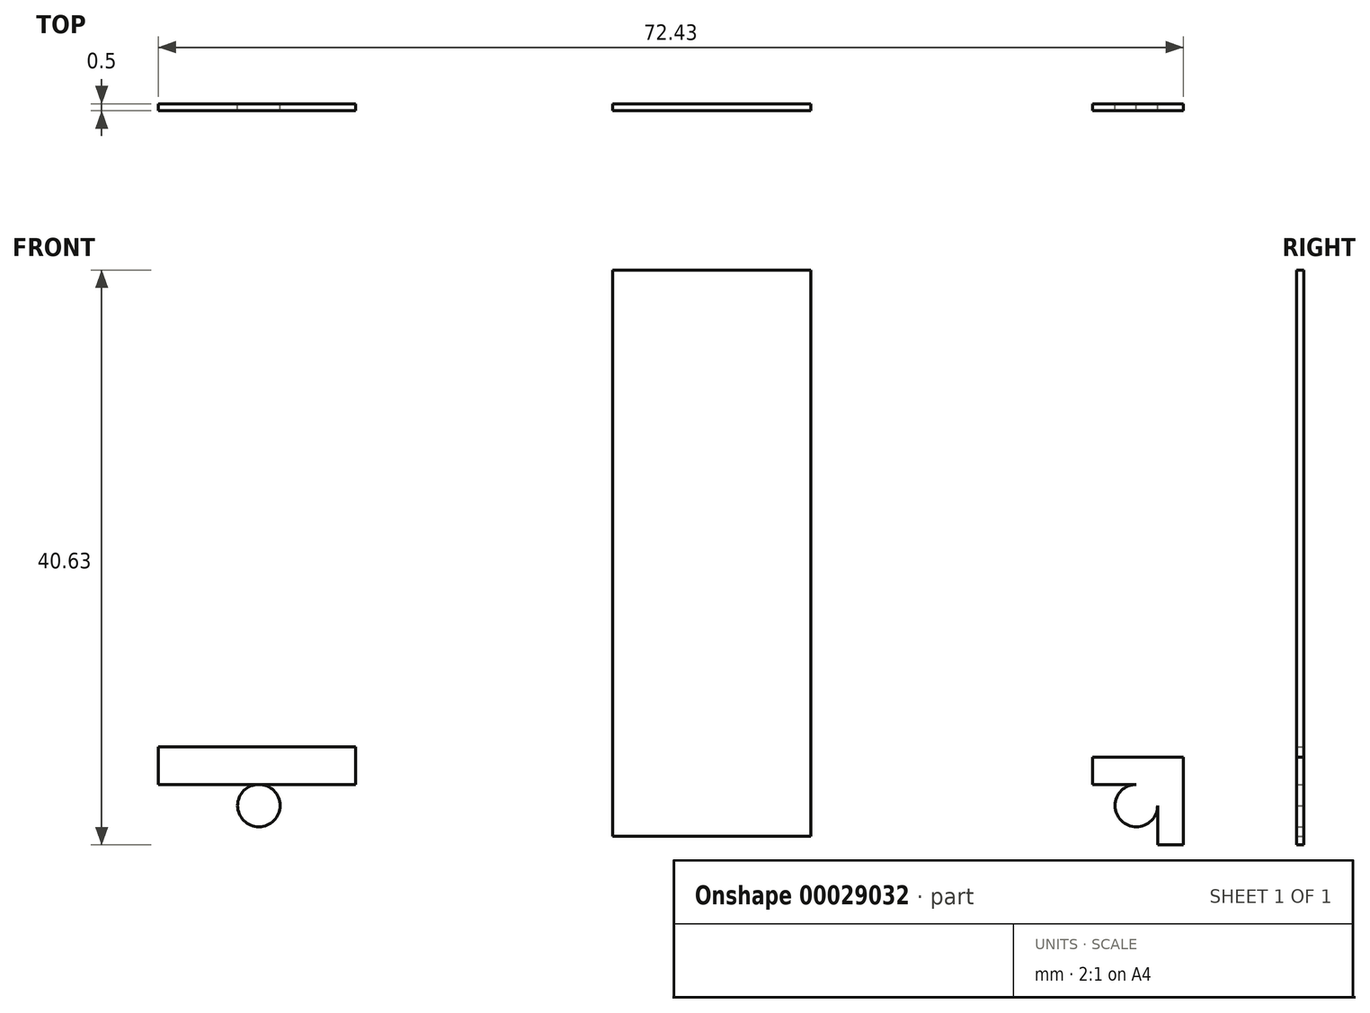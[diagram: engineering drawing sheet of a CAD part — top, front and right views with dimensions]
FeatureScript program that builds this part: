
annotation { "Feature Type Name" : "Feature", "Feature Type Description" : "" }
export const myFeature = defineFeature(function(context is Context, id is Id, definition is map)
    precondition{}
    {
        {
            var Q0;
            Q0=qCreatedBy(makeId("Front.planeOp"),FACE);
            var sketch = newSketch(context, id + "F0", { "sketchPlane" : qUnion([Q0])});
            skCircle(sketch, "E0", {"center": v(23, -33.75) * mm, "radius": 1.5 * mm});
            skCircle(sketch, "E1", {"center": v(-39, -33.75) * mm, "radius": 1.5 * mm});
            skLineSegment(sketch, "E2", {"start": v(24.5, -36.53) * mm, "end": v(24.5, -32.25) * mm});
            skLineSegment(sketch, "E3", {"start": v(24.5, -32.25) * mm, "end": v(19.9, -32.25) * mm});
            skLineSegment(sketch, "E4", {"start": v(19.9, -32.25) * mm, "end": v(19.9, -30.34) * mm});
            skLineSegment(sketch, "E5", {"start": v(19.9, -30.34) * mm, "end": v(26.32, -30.34) * mm});
            skLineSegment(sketch, "E6", {"start": v(26.32, -30.34) * mm, "end": v(26.32, -36.53) * mm});
            skLineSegment(sketch, "E7", {"start": v(26.32, -36.53) * mm, "end": v(24.5, -36.53) * mm});
            skLineSegment(sketch, "E8.bottom", {"start": v(-46.11, -29.6) * mm, "end": v(-32.17, -29.6) * mm});
            skLineSegment(sketch, "E8.top", {"start": v(-46.11, -32.25) * mm, "end": v(-32.17, -32.25) * mm});
            skLineSegment(sketch, "E8.left", {"start": v(-46.11, -29.6) * mm, "end": v(-46.11, -32.25) * mm});
            skLineSegment(sketch, "E8.right", {"start": v(-32.17, -29.6) * mm, "end": v(-32.17, -32.25) * mm});
            skLineSegment(sketch, "E9.bottom", {"start": v(0, 4.1) * mm, "end": v(-14, 4.1) * mm});
            skLineSegment(sketch, "E9.top", {"start": v(0, -35.9) * mm, "end": v(-14, -35.9) * mm});
            skLineSegment(sketch, "E9.left", {"start": v(0, 4.1) * mm, "end": v(0, -35.9) * mm});
            skLineSegment(sketch, "E9.right", {"start": v(-14, 4.1) * mm, "end": v(-14, -35.9) * mm});
            skLineSegment(sketch, "E10", {"start": v(-10.45, -15.9) * mm, "end": v(-2.77, -15.9) * mm});
            skLineSegment(sketch, "E11", {"start": v(-7, -13.12) * mm, "end": v(-7, -18.9) * mm});
            skSolve(sketch);
        }
        {
            var Q0;
            Q0=qSketchRegion(id+"F0",true);
            extrude(context, id + "F1", {"entities" : qUnion([Q0]), "depth" : .5 * mm});
        }
    });
